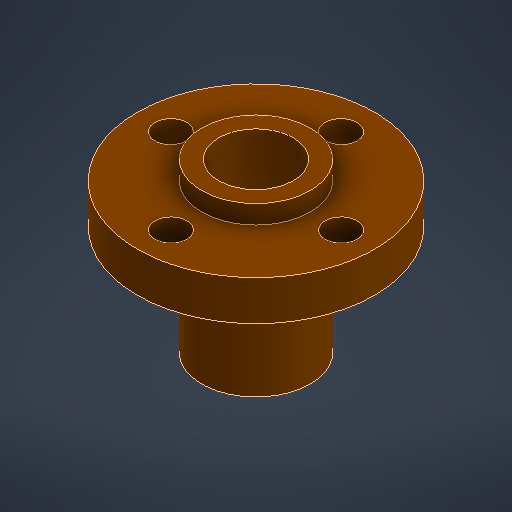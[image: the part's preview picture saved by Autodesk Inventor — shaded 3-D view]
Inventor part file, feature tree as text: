
AUTODESK INVENTOR PART (.ipt)
format: ipt  version: 2025.1 (Build 291241000, 241)  size: 230,912 bytes
history: native  units: mm
features: extrude x3, sketch x2
ambient origin geometry x8: Origin, YZ Plane, XZ Plane, XY Plane, X Axis, Y Axis, Z Axis, Center Point
bodies: Solid1 (feature_tree)
feature tree (5):
  sketch  "Sketch1"  dims[d0=22.3mm d1=7.0mm]
  extrude  "Extrusion1"  Depth=7.0mm
  extrude  "Extrusion2"  Depth=8.0mm
  extrude  "Extrusion3"  Depth=10.25mm TaperAngle=360.0deg
  sketch  "Sketch Circular Pattern1"  dims[d2=3.0mm d3=8.0mm d4=40.0mm d6=360.0deg d8=10.2mm d9=3.75mm d10=0.0mm d11=1.75mm d12=0.0mm d13=10.25mm d14=0.0mm]
